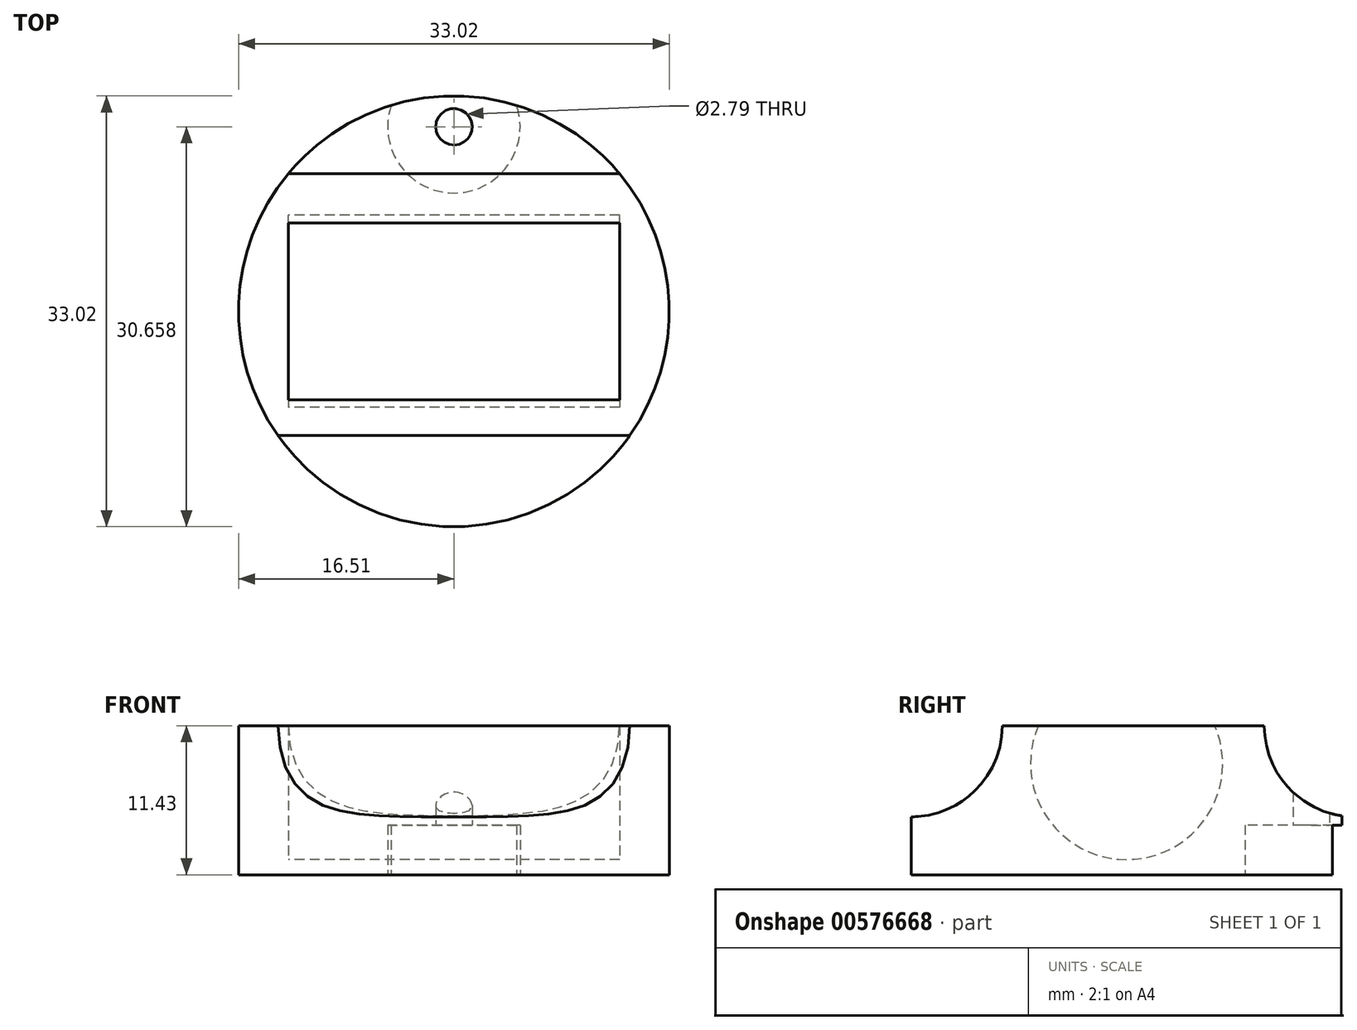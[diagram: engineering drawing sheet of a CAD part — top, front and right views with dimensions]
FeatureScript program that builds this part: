
annotation { "Feature Type Name" : "Feature", "Feature Type Description" : "" }
export const myFeature = defineFeature(function(context is Context, id is Id, definition is map)
    precondition{}
    {
        {
            var Q0;
            Q0=qCreatedBy(makeId("Top.planeOp"),FACE);
            var sketch = newSketch(context, id + "F0", { "sketchPlane" : qUnion([Q0])});
            skCircle(sketch, "E0", {"center": v(0, 0) * mm, "radius": 16.51 * mm});
            skSolve(sketch);
        }
        {
            var Q0;
            Q0=makeQuery(id+"F0.imprint","IMPRINT",FACE,{"disambiguationData":[TD([[makeQuery(id+"F0.imprint","IMPRINT",EDGE,{"derivedFrom":sQuery(id+"F0.wireOp",EDGE,"E0")}),1.0]])]});
            var Q1;
            Q1=sQuery(id+"F0.wireOp",EDGE,"E0");
            extrude(context, id + "F1", {"entities" : qUnion([Q0]), "surfaceEntities" : qUnion([Q1]), "depth" : 11.43 * mm, "offsetDistance" : 25.4 * mm});
        }
        {
            var Q0;
            Q0=qCreatedBy(makeId("Right.planeOp"),FACE);
            var sketch = newSketch(context, id + "F2", { "sketchPlane" : qUnion([Q0])});
            skLineSegment(sketch, "E1", {"start": v(0, 0) * mm, "end": v(0, 8.53) * mm});
            skCircle(sketch, "E2", {"center": v(0, 8.53) * mm, "radius": 7.37 * mm});
            skSolve(sketch);
        }
        {
            var Q0;
            Q0=makeQuery(id+"F2.imprint","IMPRINT",FACE,{"disambiguationData":[TD([[makeQuery(id+"F2.imprint","IMPRINT",EDGE,{"derivedFrom":sQuery(id+"F2.wireOp",EDGE,"E2")}),1.0]])]});
            extrude(context, id + "F3", {"entities" : qUnion([Q0]), "operationType" : NewBodyOperationType.REMOVE, "endBound" : BoundingType.SYMMETRIC, "depth" : 25.4 * mm, "offsetDistance" : 25.4 * mm});
        }
        {
            var Q0;
            Q0=qCreatedBy(makeId("Top.planeOp"),FACE);
            var sketch = newSketch(context, id + "F4", { "sketchPlane" : qUnion([Q0])});
            skLineSegment(sketch, "E3", {"start": v(0, 0) * mm, "end": v(0, 14.15) * mm});
            skCircle(sketch, "E4", {"center": v(0, 14.15) * mm, "radius": 5.08 * mm});
            skSolve(sketch);
        }
        {
            var Q0;
            Q0=makeQuery(id+"F4.imprint","IMPRINT",FACE,{"disambiguationData":[TD([[makeQuery(id+"F4.imprint","IMPRINT",EDGE,{"derivedFrom":sQuery(id+"F4.wireOp",EDGE,"E4")}),1.0]])]});
            extrude(context, id + "F5", {"entities" : qUnion([Q0]), "operationType" : NewBodyOperationType.REMOVE, "depth" : 3.8 * mm, "offsetDistance" : 25.4 * mm});
        }
        {
            var Q0;
            Q0=qCreatedBy(makeId("Top.planeOp"),FACE);
            var sketch = newSketch(context, id + "F6", { "sketchPlane" : qUnion([Q0])});
            skLineSegment(sketch, "E5", {"start": v(0, 0) * mm, "end": v(0, 14.15) * mm});
            skCircle(sketch, "E6", {"center": v(0, 14.15) * mm, "radius": 1.4 * mm});
            skSolve(sketch);
        }
        {
            var Q0;
            Q0=makeQuery(id+"F6.imprint","IMPRINT",FACE,{"disambiguationData":[TD([[makeQuery(id+"F6.imprint","IMPRINT",EDGE,{"derivedFrom":sQuery(id+"F6.wireOp",EDGE,"E6")}),1.0]])]});
            var Q1;
            Q1=makeQuery(id+"F1.opExtrude","CAP_FACE",FACE,{"disambiguationData":[OSD([sQuery(id+"F0.wireOp",EDGE,"E0")])],"isStart":false});
            extrude(context, id + "F7", {"entities" : qUnion([Q0]), "operationType" : NewBodyOperationType.REMOVE, "endBound" : BoundingType.UP_TO_SURFACE, "depth" : 25.4 * mm, "endBoundEntityFace" : qUnion([Q1]), "offsetDistance" : 25.4 * mm});
        }
        {
            var Q0;
            Q0=qCreatedBy(makeId("Right.planeOp"),FACE);
            var sketch = newSketch(context, id + "F8", { "sketchPlane" : qUnion([Q0])});
            skLineSegment(sketch, "E7", {"start": v(0, 0) * mm, "end": v(-16.51, 0) * mm});
            skLineSegment(sketch, "E8", {"start": v(-16.51, 0) * mm, "end": v(-16.51, 11.43) * mm});
            skCircle(sketch, "E9", {"center": v(-16.51, 11.43) * mm, "radius": 6.99 * mm});
            skSolve(sketch);
        }
        {
            var Q0;
            Q0=makeQuery(id+"F8.imprint","IMPRINT",FACE,{"disambiguationData":[TD([[makeQuery(id+"F8.imprint","IMPRINT",EDGE,{"derivedFrom":sQuery(id+"F8.wireOp",EDGE,"E9")}),1.0]])]});
            extrude(context, id + "F9", {"entities" : qUnion([Q0]), "operationType" : NewBodyOperationType.REMOVE, "endBound" : BoundingType.SYMMETRIC, "oppositeDirection" : true, "depth" : 50.8 * mm, "offsetDistance" : 25.4 * mm});
        }
        {
            var Q0;
            Q0=qCreatedBy(makeId("Right.planeOp"),FACE);
            var sketch = newSketch(context, id + "F10", { "sketchPlane" : qUnion([Q0])});
            skLineSegment(sketch, "E10", {"start": v(0, 0) * mm, "end": v(16.51, 0) * mm});
            skLineSegment(sketch, "E11", {"start": v(16.51, 0) * mm, "end": v(16.51, 11.43) * mm});
            skCircle(sketch, "E12", {"center": v(17.53, 11.43) * mm, "radius": 6.99 * mm});
            skSolve(sketch);
        }
        {
            var Q0;
            Q0=makeQuery(id+"F10.imprint","IMPRINT",FACE,{"disambiguationData":[TD([[makeQuery(id+"F10.imprint","IMPRINT",EDGE,{"derivedFrom":sQuery(id+"F10.wireOp",EDGE,"E12")}),1.0]])]});
            extrude(context, id + "F11", {"entities" : qUnion([Q0]), "operationType" : NewBodyOperationType.REMOVE, "endBound" : BoundingType.SYMMETRIC, "oppositeDirection" : true, "depth" : 50.8 * mm, "offsetDistance" : 25.4 * mm});
        }
    });
